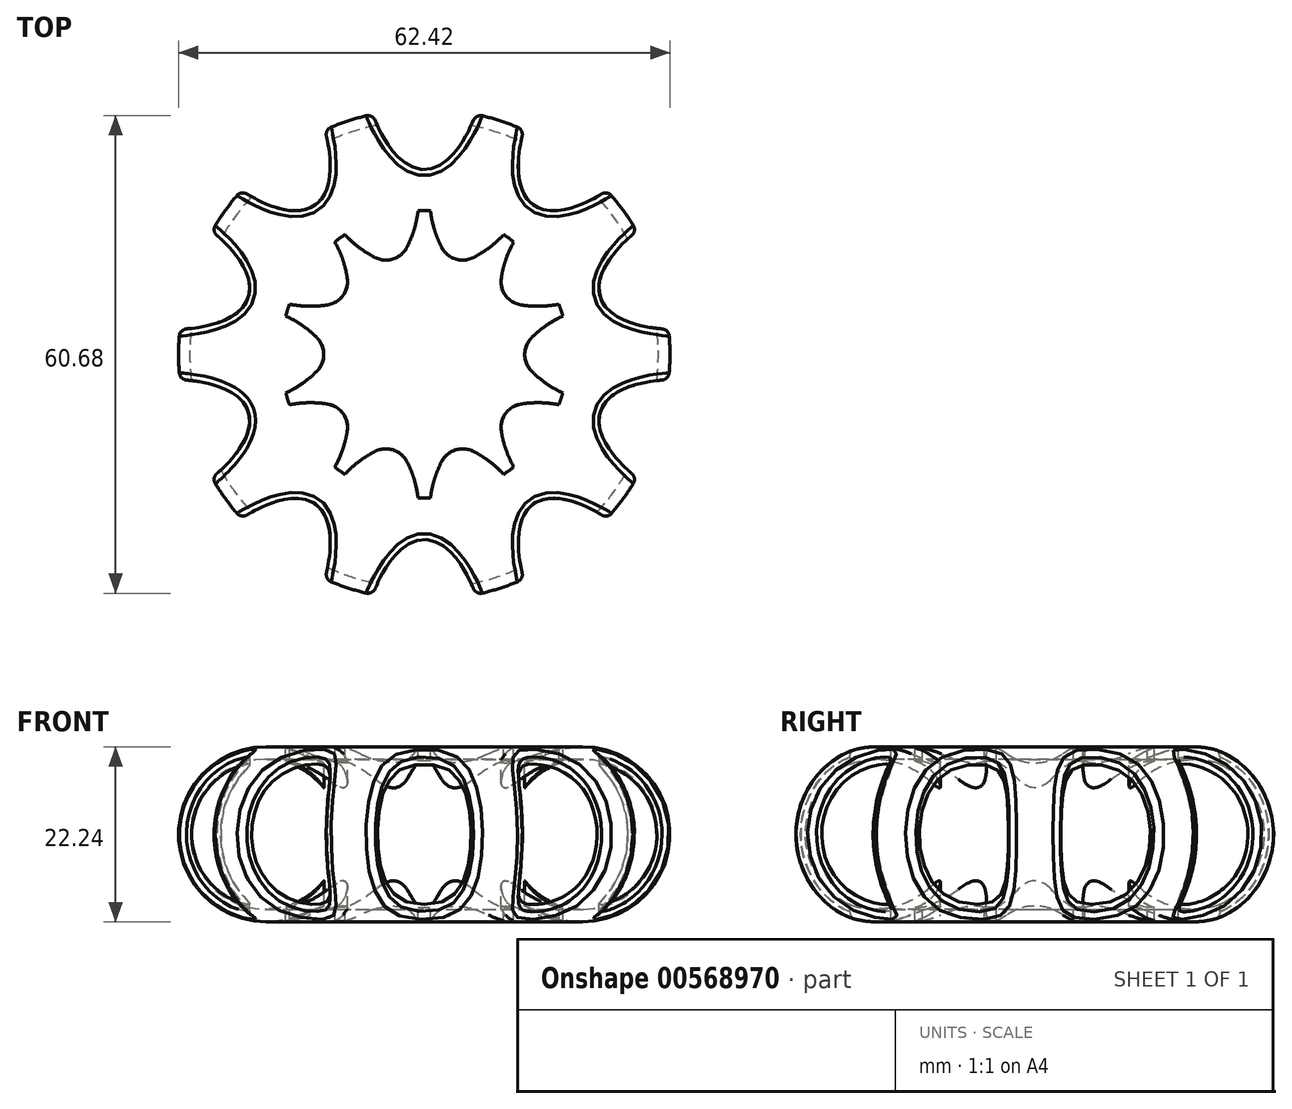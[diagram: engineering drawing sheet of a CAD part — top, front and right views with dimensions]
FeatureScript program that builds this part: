
annotation { "Feature Type Name" : "Feature", "Feature Type Description" : "" }
export const myFeature = defineFeature(function(context is Context, id is Id, definition is map)
    precondition{}
    {
        {
            var Q0;
            Q0=qCreatedBy(makeId("Front.planeOp"),FACE);
            var sketch = newSketch(context, id + "F0", { "sketchPlane" : qUnion([Q0])});
            skArc(sketch, "E0", {"start": v(-15.71, 10.22) * mm, "mid": v(-31.2, 0.04) * mm, "end": v(-15.8, -10.25) * mm});
            skArc(sketch, "E1", {"start": v(-15.71, 10.22) * mm, "mid": v(-8.02, 7.81) * mm, "end": v(0, 7) * mm});
            skArc(sketch, "E2", {"start": v(0, -7) * mm, "mid": v(-8.05, -7.86) * mm, "end": v(-15.8, -10.25) * mm});
            skLineSegment(sketch, "E3", {"start": v(0, -7) * mm, "end": v(0, 7) * mm});
            skSolve(sketch);
        }
        {
            var Q0;
            Q0 = qSketchRegion(id + "F0", true);
            var Q1;
            Q1=sQuery(id+"F0.wireOp",EDGE,"E3");
            revolve(context, id + "F1", {"entities" : qUnion([Q0]), "axis" : qUnion([Q1]), "revolveType" : RevolveType.FULL});
        }
        {
            var Q0;
            Q0=qCreatedBy(makeId("Top.planeOp"),FACE);
            cPlane(context, id + "F2", {"entities" : qUnion([Q0]), "cplaneType" : CPlaneType.OFFSET, "offset" : 12.5 * mm, "width" : 150 * mm, "height" : 150 * mm});
        }
        {
            var Q0;
            Q0=qCreatedBy(id+"F2.planeOp",FACE);
            var sketch = newSketch(context, id + "F3", { "sketchPlane" : qUnion([Q0])});
            skCircle(sketch, "E4", {"center": v(0, 0) * mm, "radius": 18.26 * mm});
            skArc(sketch, "E5", {"start": v(-10.09, 15.22) * mm, "mid": v(-7.15, 12.83) * mm, "end": v(-3.68, 11.32) * mm});
            skArc(sketch, "E6.1.1", {"start": v(-17.1, 6.39) * mm, "mid": v(-13.33, 6.17) * mm, "end": v(-9.63, 7) * mm});
            skArc(sketch, "E6.2.1", {"start": v(-17.6, -4.89) * mm, "mid": v(-14.41, -2.84) * mm, "end": v(-11.9, 0) * mm});
            skArc(sketch, "E6.3.1", {"start": v(-11.36, -14.3) * mm, "mid": v(-9.99, -10.77) * mm, "end": v(-9.63, -7) * mm});
            skArc(sketch, "E6.4.1", {"start": v(-0.79, -18.25) * mm, "mid": v(-1.75, -14.58) * mm, "end": v(-3.68, -11.32) * mm});
            skArc(sketch, "E6.5.1", {"start": v(10.09, -15.22) * mm, "mid": v(7.15, -12.83) * mm, "end": v(3.68, -11.32) * mm});
            skArc(sketch, "E6.6.1", {"start": v(17.1, -6.39) * mm, "mid": v(13.33, -6.17) * mm, "end": v(9.63, -7) * mm});
            skArc(sketch, "E6.7.1", {"start": v(17.6, 4.89) * mm, "mid": v(14.41, 2.84) * mm, "end": v(11.9, 0) * mm});
            skArc(sketch, "E6.8.1", {"start": v(11.36, 14.3) * mm, "mid": v(9.99, 10.77) * mm, "end": v(9.63, 7) * mm});
            skArc(sketch, "E6.9.1", {"start": v(0.79, 18.25) * mm, "mid": v(1.75, 14.58) * mm, "end": v(3.68, 11.32) * mm});
            skArc(sketch, "E7.trimOffspring", {"start": v(-3.68, 11.32) * mm, "mid": v(-1.75, 14.58) * mm, "end": v(-0.79, 18.25) * mm});
            skArc(sketch, "E8.trimOffspring", {"start": v(3.68, 11.32) * mm, "mid": v(7.15, 12.83) * mm, "end": v(10.09, 15.22) * mm});
            skArc(sketch, "E9.trimOffspring", {"start": v(9.63, 7) * mm, "mid": v(13.33, 6.17) * mm, "end": v(17.1, 6.39) * mm});
            skArc(sketch, "E10.trimOffspring", {"start": v(11.9, 0) * mm, "mid": v(14.41, -2.84) * mm, "end": v(17.6, -4.89) * mm});
            skArc(sketch, "E11.trimOffspring", {"start": v(9.63, -7) * mm, "mid": v(9.99, -10.77) * mm, "end": v(11.36, -14.3) * mm});
            skArc(sketch, "E12.trimOffspring", {"start": v(3.68, -11.32) * mm, "mid": v(1.75, -14.58) * mm, "end": v(0.79, -18.25) * mm});
            skArc(sketch, "E13.trimOffspring", {"start": v(-3.68, -11.32) * mm, "mid": v(-7.15, -12.83) * mm, "end": v(-10.09, -15.22) * mm});
            skArc(sketch, "E14.trimOffspring", {"start": v(-9.63, -7) * mm, "mid": v(-13.33, -6.17) * mm, "end": v(-17.1, -6.39) * mm});
            skArc(sketch, "E15.trimOffspring", {"start": v(-11.9, 0) * mm, "mid": v(-14.41, 2.84) * mm, "end": v(-17.6, 4.89) * mm});
            skArc(sketch, "E16.trimOffspring", {"start": v(-9.63, 7) * mm, "mid": v(-9.99, 10.77) * mm, "end": v(-11.36, 14.3) * mm});
            skSolve(sketch);
        }
        {
            var Q0;
            {var subQ7=sQuery(id+"F3.wireOp",EDGE,"E5");Q0=makeQuery(id+"F3.imprint","IMPRINT",FACE,{"disambiguationData":[TD([[makeQuery(id+"F3.imprint","IMPRINT",EDGE,{"derivedFrom":subQ7}),-1.0]])]});}
            extrude(context, id + "F4", {"entities" : qUnion([Q0]), "operationType" : NewBodyOperationType.REMOVE, "oppositeDirection" : true, "depth" : 25 * mm, "offsetDistance" : 25 * mm});
        }
        {
            var Q0;
            Q0=qCreatedBy(id+"F2.planeOp",FACE);
            var sketch = newSketch(context, id + "F5", { "sketchPlane" : qUnion([Q0])});
            skCircle(sketch, "E17", {"center": v(0, 0) * mm, "radius": 31.42 * mm});
            skEllipticalArc(sketch, "E18", {});
            skEllipticalArc(sketch, "E19.1.0", {});
            skEllipticalArc(sketch, "E19.2.0", {});
            skEllipticalArc(sketch, "E19.3.0", {});
            skEllipticalArc(sketch, "E19.4.0", {});
            skEllipticalArc(sketch, "E19.5.0", {});
            skEllipticalArc(sketch, "E19.6.0", {});
            skEllipticalArc(sketch, "E19.7.0", {});
            skEllipticalArc(sketch, "E19.8.0", {});
            skEllipticalArc(sketch, "E19.9.0", {});
            const initialGuessF5  = {"E18": [0, 0.04669829085469246, 0, -1, 0.02319059520959854, 0.009151522777861269, 5.472659938660135, 0.8105253685194521], "E19.1.0": [-0.0274485666716527, 0.03777971090971039, 0.5877852522924731, -0.8090169943749475, 0.02319059520959854, 0.009151522777861269, 5.472659938660135, 0.8105253685194521], "E19.2.0": [-0.04441271381720164, 0.01443056548236416, 0.9510565162951538, -0.3090169943749475, 0.02319059520959854, 0.009151522777861269, 5.472659938660135, 0.8105253685194521], "E19.3.0": [-0.044412713817201646, -0.014430565482364155, 0.9510565162951536, 0.30901699437494734, 0.02319059520959854, 0.009151522777861269, 5.472659938660135, 0.8105253685194521], "E19.4.0": [-0.027448566671652703, -0.037779710909710384, 0.5877852522924732, 0.8090169943749473, 0.02319059520959854, 0.009151522777861269, 5.472659938660135, 0.8105253685194521], "E19.5.0": [0, -0.04669829085469246, 0, 1, 0.02319059520959854, 0.009151522777861269, 5.472659938660135, 0.8105253685194521], "E19.6.0": [0.027448566671652692, -0.03777971090971039, -0.587785252292473, 0.8090169943749476, 0.02319059520959854, 0.009151522777861269, 5.472659938660135, 0.8105253685194521], "E19.7.0": [0.04441271381720164, -0.014430565482364165, -0.9510565162951535, 0.30901699437494756, 0.02319059520959854, 0.009151522777861269, 5.472659938660135, 0.8105253685194521], "E19.8.0": [0.044412713817201646, 0.01443056548236415, -0.9510565162951536, -0.30901699437494723, 0.02319059520959854, 0.009151522777861269, 5.472659938660135, 0.8105253685194521], "E19.9.0": [0.02744856667165271, 0.037779710909710384, -0.5877852522924734, -0.8090169943749473, 0.02319059520959854, 0.009151522777861269, 5.472659938660135, 0.8105253685194521]};
            skSetInitialGuess(sketch, initialGuessF5);
            skSolve(sketch);
        }
        {
            var Q0;
            {var subQ0=sQuery(id+"F5.wireOp",EDGE,"E18");Q0=makeQuery(id+"F5.imprint","IMPRINT",FACE,{"disambiguationData":[TD([[makeQuery(id+"F5.imprint","IMPRINT",EDGE,{"derivedFrom":subQ0}),1.0]])]});}
            var Q1;
            {var subQ0=sQuery(id+"F5.wireOp",EDGE,"E19.9.0");Q1=makeQuery(id+"F5.imprint","IMPRINT",FACE,{"disambiguationData":[TD([[makeQuery(id+"F5.imprint","IMPRINT",EDGE,{"derivedFrom":subQ0}),1.0]])]});}
            var Q2;
            {var subQ0=sQuery(id+"F5.wireOp",EDGE,"E19.8.0");Q2=makeQuery(id+"F5.imprint","IMPRINT",FACE,{"disambiguationData":[TD([[makeQuery(id+"F5.imprint","IMPRINT",EDGE,{"derivedFrom":subQ0}),1.0]])]});}
            var Q3;
            {var subQ0=sQuery(id+"F5.wireOp",EDGE,"E19.7.0");Q3=makeQuery(id+"F5.imprint","IMPRINT",FACE,{"disambiguationData":[TD([[makeQuery(id+"F5.imprint","IMPRINT",EDGE,{"derivedFrom":subQ0}),1.0]])]});}
            var Q4;
            {var subQ0=sQuery(id+"F5.wireOp",EDGE,"E19.6.0");Q4=makeQuery(id+"F5.imprint","IMPRINT",FACE,{"disambiguationData":[TD([[makeQuery(id+"F5.imprint","IMPRINT",EDGE,{"derivedFrom":subQ0}),1.0]])]});}
            var Q5;
            {var subQ0=sQuery(id+"F5.wireOp",EDGE,"E19.5.0");Q5=makeQuery(id+"F5.imprint","IMPRINT",FACE,{"disambiguationData":[TD([[makeQuery(id+"F5.imprint","IMPRINT",EDGE,{"derivedFrom":subQ0}),1.0]])]});}
            var Q6;
            {var subQ0=sQuery(id+"F5.wireOp",EDGE,"E19.4.0");Q6=makeQuery(id+"F5.imprint","IMPRINT",FACE,{"disambiguationData":[TD([[makeQuery(id+"F5.imprint","IMPRINT",EDGE,{"derivedFrom":subQ0}),1.0]])]});}
            var Q7;
            {var subQ0=sQuery(id+"F5.wireOp",EDGE,"E19.3.0");Q7=makeQuery(id+"F5.imprint","IMPRINT",FACE,{"disambiguationData":[TD([[makeQuery(id+"F5.imprint","IMPRINT",EDGE,{"derivedFrom":subQ0}),1.0]])]});}
            var Q8;
            {var subQ0=sQuery(id+"F5.wireOp",EDGE,"E19.2.0");Q8=makeQuery(id+"F5.imprint","IMPRINT",FACE,{"disambiguationData":[TD([[makeQuery(id+"F5.imprint","IMPRINT",EDGE,{"derivedFrom":subQ0}),1.0]])]});}
            var Q9;
            {var subQ0=sQuery(id+"F5.wireOp",EDGE,"E19.1.0");Q9=makeQuery(id+"F5.imprint","IMPRINT",FACE,{"disambiguationData":[TD([[makeQuery(id+"F5.imprint","IMPRINT",EDGE,{"derivedFrom":subQ0}),1.0]])]});}
            extrude(context, id + "F6", {"entities" : qUnion([Q0, Q1, Q2, Q3, Q4, Q5, Q6, Q7, Q8, Q9]), "operationType" : NewBodyOperationType.REMOVE, "oppositeDirection" : true, "depth" : 25 * mm, "offsetDistance" : 25 * mm});
        }
        {
            var Q0;
            Q0=qCreatedBy(makeId("Front.planeOp"),FACE);
            var sketch = newSketch(context, id + "F7", { "sketchPlane" : qUnion([Q0])});
            skCircle(sketch, "E20", {"center": v(-20.22, 0) * mm, "radius": 9.51 * mm});
            skSolve(sketch);
        }
        {
            var Q0;
            Q0 = qSketchRegion(id + "F7", true);
            var Q1;
            Q1=sQuery(id+"F0.wireOp",EDGE,"E3");
            revolve(context, id + "F8", {"operationType" : NewBodyOperationType.REMOVE, "entities" : qUnion([Q0]), "axis" : qUnion([Q1]), "revolveType" : RevolveType.FULL});
        }
        {
            var Q0;
            Q0=makeQuery(id+"F6.boolean.opBoolean","INTERSECT",EDGE,{"derivedFrom":[makeQuery(id+"F1.opRevolve","SWEPT_FACE",FACE,{"disambiguationData":[OSD([sQuery(id+"F0.wireOp",EDGE,"E0")])]}),makeQuery(id+"F6.opExtrude","SWEPT_FACE",FACE,{"disambiguationData":[OSD([sQuery(id+"F5.wireOp",EDGE,"E19.6.0")])]})]});
            var Q1;
            Q1=makeQuery(id+"F6.boolean.opBoolean","INTERSECT",EDGE,{"derivedFrom":[makeQuery(id+"F1.opRevolve","SWEPT_FACE",FACE,{"disambiguationData":[OSD([sQuery(id+"F0.wireOp",EDGE,"E0")])]}),makeQuery(id+"F6.opExtrude","SWEPT_FACE",FACE,{"disambiguationData":[OSD([sQuery(id+"F5.wireOp",EDGE,"E19.5.0")])]})]});
            var Q2;
            Q2=makeQuery(id+"F6.boolean.opBoolean","INTERSECT",EDGE,{"derivedFrom":[makeQuery(id+"F1.opRevolve","SWEPT_FACE",FACE,{"disambiguationData":[OSD([sQuery(id+"F0.wireOp",EDGE,"E0")])]}),makeQuery(id+"F6.opExtrude","SWEPT_FACE",FACE,{"disambiguationData":[OSD([sQuery(id+"F5.wireOp",EDGE,"E19.4.0")])]})]});
            var Q3;
            Q3=makeQuery(id+"F6.boolean.opBoolean","INTERSECT",EDGE,{"derivedFrom":[makeQuery(id+"F1.opRevolve","SWEPT_FACE",FACE,{"disambiguationData":[OSD([sQuery(id+"F0.wireOp",EDGE,"E0")])]}),makeQuery(id+"F6.opExtrude","SWEPT_FACE",FACE,{"disambiguationData":[OSD([sQuery(id+"F5.wireOp",EDGE,"E19.3.0")])]})]});
            var Q4;
            Q4=makeQuery(id+"F6.boolean.opBoolean","INTERSECT",EDGE,{"derivedFrom":[makeQuery(id+"F1.opRevolve","SWEPT_FACE",FACE,{"disambiguationData":[OSD([sQuery(id+"F0.wireOp",EDGE,"E0")])]}),makeQuery(id+"F6.opExtrude","SWEPT_FACE",FACE,{"disambiguationData":[OSD([sQuery(id+"F5.wireOp",EDGE,"E19.2.0")])]})]});
            var Q5;
            Q5=makeQuery(id+"F6.boolean.opBoolean","INTERSECT",EDGE,{"derivedFrom":[makeQuery(id+"F1.opRevolve","SWEPT_FACE",FACE,{"disambiguationData":[OSD([sQuery(id+"F0.wireOp",EDGE,"E0")])]}),makeQuery(id+"F6.opExtrude","SWEPT_FACE",FACE,{"disambiguationData":[OSD([sQuery(id+"F5.wireOp",EDGE,"E19.1.0")])]})]});
            var Q6;
            Q6=makeQuery(id+"F6.boolean.opBoolean","INTERSECT",EDGE,{"derivedFrom":[makeQuery(id+"F1.opRevolve","SWEPT_FACE",FACE,{"disambiguationData":[OSD([sQuery(id+"F0.wireOp",EDGE,"E0")])]}),makeQuery(id+"F6.opExtrude","SWEPT_FACE",FACE,{"disambiguationData":[OSD([sQuery(id+"F5.wireOp",EDGE,"E18")])]})]});
            var Q7;
            Q7=makeQuery(id+"F6.boolean.opBoolean","INTERSECT",EDGE,{"derivedFrom":[makeQuery(id+"F1.opRevolve","SWEPT_FACE",FACE,{"disambiguationData":[OSD([sQuery(id+"F0.wireOp",EDGE,"E0")])]}),makeQuery(id+"F6.opExtrude","SWEPT_FACE",FACE,{"disambiguationData":[OSD([sQuery(id+"F5.wireOp",EDGE,"E19.9.0")])]})]});
            var Q8;
            Q8=makeQuery(id+"F6.boolean.opBoolean","INTERSECT",EDGE,{"derivedFrom":[makeQuery(id+"F1.opRevolve","SWEPT_FACE",FACE,{"disambiguationData":[OSD([sQuery(id+"F0.wireOp",EDGE,"E0")])]}),makeQuery(id+"F6.opExtrude","SWEPT_FACE",FACE,{"disambiguationData":[OSD([sQuery(id+"F5.wireOp",EDGE,"E19.8.0")])]})]});
            var Q9;
            Q9=makeQuery(id+"F6.boolean.opBoolean","INTERSECT",EDGE,{"derivedFrom":[makeQuery(id+"F1.opRevolve","SWEPT_FACE",FACE,{"disambiguationData":[OSD([sQuery(id+"F0.wireOp",EDGE,"E0")])]}),makeQuery(id+"F6.opExtrude","SWEPT_FACE",FACE,{"disambiguationData":[OSD([sQuery(id+"F5.wireOp",EDGE,"E19.7.0")])]})]});
            fillet(context, id + "F9", {"entities" : qUnion([Q0, Q1, Q2, Q3, Q4, Q5, Q6, Q7, Q8, Q9]), "radius" : 1 * mm, "tangentPropagation" : true, "allowEdgeOverflow" : false});
        }
        {
            var Q0;
            {var subQ0=sQuery(id+"F3.wireOp",EDGE,"E6.3.1");var subQ1=sQuery(id+"F3.wireOp",EDGE,"E14.trimOffspring");Q0=makeQuery(id+"F8.boolean.opBoolean","SPLIT",EDGE,{"disambiguationData":[TD([makeQuery(id+"F1.opRevolve","SWEPT_FACE",FACE,{"disambiguationData":[OSD([sQuery(id+"F0.wireOp",EDGE,"E1")])]})])],"derivedFrom":makeQuery(id+"F4.boolean.opBoolean","COPY",EDGE,{"derivedFrom":makeQuery(id+"F4.opExtrude","SWEPT_EDGE",EDGE,{"disambiguationData":[OSD([subQ0,subQ1])]})})});}
            var Q1;
            {var subQ0=sQuery(id+"F3.wireOp",EDGE,"E13.trimOffspring");var subQ1=sQuery(id+"F3.wireOp",EDGE,"E6.4.1");Q1=makeQuery(id+"F8.boolean.opBoolean","SPLIT",EDGE,{"disambiguationData":[TD([makeQuery(id+"F1.opRevolve","SWEPT_FACE",FACE,{"disambiguationData":[OSD([sQuery(id+"F0.wireOp",EDGE,"E1")])]})])],"derivedFrom":makeQuery(id+"F4.boolean.opBoolean","COPY",EDGE,{"derivedFrom":makeQuery(id+"F4.opExtrude","SWEPT_EDGE",EDGE,{"disambiguationData":[OSD([subQ1,subQ0])]})})});}
            var Q2;
            {var subQ0=sQuery(id+"F3.wireOp",EDGE,"E6.2.1");var subQ1=sQuery(id+"F3.wireOp",EDGE,"E15.trimOffspring");Q2=makeQuery(id+"F8.boolean.opBoolean","SPLIT",EDGE,{"disambiguationData":[TD([makeQuery(id+"F1.opRevolve","SWEPT_FACE",FACE,{"disambiguationData":[OSD([sQuery(id+"F0.wireOp",EDGE,"E1")])]})])],"derivedFrom":makeQuery(id+"F4.boolean.opBoolean","COPY",EDGE,{"derivedFrom":makeQuery(id+"F4.opExtrude","SWEPT_EDGE",EDGE,{"disambiguationData":[OSD([subQ0,subQ1])]})})});}
            var Q3;
            {var subQ0=sQuery(id+"F3.wireOp",EDGE,"E6.1.1");var subQ1=sQuery(id+"F3.wireOp",EDGE,"E16.trimOffspring");Q3=makeQuery(id+"F8.boolean.opBoolean","SPLIT",EDGE,{"disambiguationData":[TD([makeQuery(id+"F1.opRevolve","SWEPT_FACE",FACE,{"disambiguationData":[OSD([sQuery(id+"F0.wireOp",EDGE,"E1")])]})])],"derivedFrom":makeQuery(id+"F4.boolean.opBoolean","COPY",EDGE,{"derivedFrom":makeQuery(id+"F4.opExtrude","SWEPT_EDGE",EDGE,{"disambiguationData":[OSD([subQ0,subQ1])]})})});}
            var Q4;
            {var subQ0=sQuery(id+"F3.wireOp",EDGE,"E5");var subQ1=sQuery(id+"F3.wireOp",EDGE,"E7.trimOffspring");Q4=makeQuery(id+"F8.boolean.opBoolean","SPLIT",EDGE,{"disambiguationData":[TD([makeQuery(id+"F1.opRevolve","SWEPT_FACE",FACE,{"disambiguationData":[OSD([sQuery(id+"F0.wireOp",EDGE,"E1")])]})])],"derivedFrom":makeQuery(id+"F4.boolean.opBoolean","COPY",EDGE,{"derivedFrom":makeQuery(id+"F4.opExtrude","SWEPT_EDGE",EDGE,{"disambiguationData":[OSD([subQ0,subQ1])]})})});}
            var Q5;
            {var subQ0=sQuery(id+"F3.wireOp",EDGE,"E8.trimOffspring");var subQ1=sQuery(id+"F3.wireOp",EDGE,"E6.9.1");Q5=makeQuery(id+"F8.boolean.opBoolean","SPLIT",EDGE,{"disambiguationData":[TD([makeQuery(id+"F1.opRevolve","SWEPT_FACE",FACE,{"disambiguationData":[OSD([sQuery(id+"F0.wireOp",EDGE,"E1")])]})])],"derivedFrom":makeQuery(id+"F4.boolean.opBoolean","COPY",EDGE,{"derivedFrom":makeQuery(id+"F4.opExtrude","SWEPT_EDGE",EDGE,{"disambiguationData":[OSD([subQ1,subQ0])]})})});}
            var Q6;
            {var subQ0=sQuery(id+"F3.wireOp",EDGE,"E6.8.1");var subQ1=sQuery(id+"F3.wireOp",EDGE,"E9.trimOffspring");Q6=makeQuery(id+"F8.boolean.opBoolean","SPLIT",EDGE,{"disambiguationData":[TD([makeQuery(id+"F1.opRevolve","SWEPT_FACE",FACE,{"disambiguationData":[OSD([sQuery(id+"F0.wireOp",EDGE,"E1")])]})])],"derivedFrom":makeQuery(id+"F4.boolean.opBoolean","COPY",EDGE,{"derivedFrom":makeQuery(id+"F4.opExtrude","SWEPT_EDGE",EDGE,{"disambiguationData":[OSD([subQ0,subQ1])]})})});}
            var Q7;
            {var subQ0=sQuery(id+"F3.wireOp",EDGE,"E6.7.1");var subQ1=sQuery(id+"F3.wireOp",EDGE,"E10.trimOffspring");Q7=makeQuery(id+"F8.boolean.opBoolean","SPLIT",EDGE,{"disambiguationData":[TD([makeQuery(id+"F1.opRevolve","SWEPT_FACE",FACE,{"disambiguationData":[OSD([sQuery(id+"F0.wireOp",EDGE,"E1")])]})])],"derivedFrom":makeQuery(id+"F4.boolean.opBoolean","COPY",EDGE,{"derivedFrom":makeQuery(id+"F4.opExtrude","SWEPT_EDGE",EDGE,{"disambiguationData":[OSD([subQ0,subQ1])]})})});}
            var Q8;
            {var subQ0=sQuery(id+"F3.wireOp",EDGE,"E6.6.1");var subQ1=sQuery(id+"F3.wireOp",EDGE,"E11.trimOffspring");Q8=makeQuery(id+"F8.boolean.opBoolean","SPLIT",EDGE,{"disambiguationData":[TD([makeQuery(id+"F1.opRevolve","SWEPT_FACE",FACE,{"disambiguationData":[OSD([sQuery(id+"F0.wireOp",EDGE,"E1")])]})])],"derivedFrom":makeQuery(id+"F4.boolean.opBoolean","COPY",EDGE,{"derivedFrom":makeQuery(id+"F4.opExtrude","SWEPT_EDGE",EDGE,{"disambiguationData":[OSD([subQ0,subQ1])]})})});}
            var Q9;
            {var subQ0=sQuery(id+"F3.wireOp",EDGE,"E6.5.1");var subQ1=sQuery(id+"F3.wireOp",EDGE,"E12.trimOffspring");Q9=makeQuery(id+"F8.boolean.opBoolean","SPLIT",EDGE,{"disambiguationData":[TD([makeQuery(id+"F1.opRevolve","SWEPT_FACE",FACE,{"disambiguationData":[OSD([sQuery(id+"F0.wireOp",EDGE,"E1")])]})])],"derivedFrom":makeQuery(id+"F4.boolean.opBoolean","COPY",EDGE,{"derivedFrom":makeQuery(id+"F4.opExtrude","SWEPT_EDGE",EDGE,{"disambiguationData":[OSD([subQ0,subQ1])]})})});}
            var Q10;
            {var subQ0=sQuery(id+"F3.wireOp",EDGE,"E6.7.1");var subQ1=sQuery(id+"F3.wireOp",EDGE,"E10.trimOffspring");Q10=makeQuery(id+"F8.boolean.opBoolean","SPLIT",EDGE,{"disambiguationData":[TD([makeQuery(id+"F1.opRevolve","SWEPT_FACE",FACE,{"disambiguationData":[OSD([sQuery(id+"F0.wireOp",EDGE,"E2")])]})])],"derivedFrom":makeQuery(id+"F4.boolean.opBoolean","COPY",EDGE,{"derivedFrom":makeQuery(id+"F4.opExtrude","SWEPT_EDGE",EDGE,{"disambiguationData":[OSD([subQ0,subQ1])]})})});}
            var Q11;
            {var subQ0=sQuery(id+"F3.wireOp",EDGE,"E6.6.1");var subQ1=sQuery(id+"F3.wireOp",EDGE,"E11.trimOffspring");Q11=makeQuery(id+"F8.boolean.opBoolean","SPLIT",EDGE,{"disambiguationData":[TD([makeQuery(id+"F1.opRevolve","SWEPT_FACE",FACE,{"disambiguationData":[OSD([sQuery(id+"F0.wireOp",EDGE,"E2")])]})])],"derivedFrom":makeQuery(id+"F4.boolean.opBoolean","COPY",EDGE,{"derivedFrom":makeQuery(id+"F4.opExtrude","SWEPT_EDGE",EDGE,{"disambiguationData":[OSD([subQ0,subQ1])]})})});}
            var Q12;
            {var subQ0=sQuery(id+"F3.wireOp",EDGE,"E6.5.1");var subQ1=sQuery(id+"F3.wireOp",EDGE,"E12.trimOffspring");Q12=makeQuery(id+"F8.boolean.opBoolean","SPLIT",EDGE,{"disambiguationData":[TD([makeQuery(id+"F1.opRevolve","SWEPT_FACE",FACE,{"disambiguationData":[OSD([sQuery(id+"F0.wireOp",EDGE,"E2")])]})])],"derivedFrom":makeQuery(id+"F4.boolean.opBoolean","COPY",EDGE,{"derivedFrom":makeQuery(id+"F4.opExtrude","SWEPT_EDGE",EDGE,{"disambiguationData":[OSD([subQ0,subQ1])]})})});}
            var Q13;
            {var subQ0=sQuery(id+"F3.wireOp",EDGE,"E9.trimOffspring");var subQ1=sQuery(id+"F3.wireOp",EDGE,"E6.8.1");Q13=makeQuery(id+"F8.boolean.opBoolean","SPLIT",EDGE,{"disambiguationData":[TD([makeQuery(id+"F1.opRevolve","SWEPT_FACE",FACE,{"disambiguationData":[OSD([sQuery(id+"F0.wireOp",EDGE,"E2")])]})])],"derivedFrom":makeQuery(id+"F4.boolean.opBoolean","COPY",EDGE,{"derivedFrom":makeQuery(id+"F4.opExtrude","SWEPT_EDGE",EDGE,{"disambiguationData":[OSD([subQ1,subQ0])]})})});}
            var Q14;
            {var subQ0=sQuery(id+"F3.wireOp",EDGE,"E6.9.1");var subQ1=sQuery(id+"F3.wireOp",EDGE,"E8.trimOffspring");Q14=makeQuery(id+"F8.boolean.opBoolean","SPLIT",EDGE,{"disambiguationData":[TD([makeQuery(id+"F1.opRevolve","SWEPT_FACE",FACE,{"disambiguationData":[OSD([sQuery(id+"F0.wireOp",EDGE,"E2")])]})])],"derivedFrom":makeQuery(id+"F4.boolean.opBoolean","COPY",EDGE,{"derivedFrom":makeQuery(id+"F4.opExtrude","SWEPT_EDGE",EDGE,{"disambiguationData":[OSD([subQ0,subQ1])]})})});}
            var Q15;
            {var subQ0=sQuery(id+"F3.wireOp",EDGE,"E6.4.1");var subQ1=sQuery(id+"F3.wireOp",EDGE,"E13.trimOffspring");Q15=makeQuery(id+"F8.boolean.opBoolean","SPLIT",EDGE,{"disambiguationData":[TD([makeQuery(id+"F1.opRevolve","SWEPT_FACE",FACE,{"disambiguationData":[OSD([sQuery(id+"F0.wireOp",EDGE,"E2")])]})])],"derivedFrom":makeQuery(id+"F4.boolean.opBoolean","COPY",EDGE,{"derivedFrom":makeQuery(id+"F4.opExtrude","SWEPT_EDGE",EDGE,{"disambiguationData":[OSD([subQ0,subQ1])]})})});}
            var Q16;
            {var subQ0=sQuery(id+"F3.wireOp",EDGE,"E14.trimOffspring");var subQ1=sQuery(id+"F3.wireOp",EDGE,"E6.3.1");Q16=makeQuery(id+"F8.boolean.opBoolean","SPLIT",EDGE,{"disambiguationData":[TD([makeQuery(id+"F1.opRevolve","SWEPT_FACE",FACE,{"disambiguationData":[OSD([sQuery(id+"F0.wireOp",EDGE,"E2")])]})])],"derivedFrom":makeQuery(id+"F4.boolean.opBoolean","COPY",EDGE,{"derivedFrom":makeQuery(id+"F4.opExtrude","SWEPT_EDGE",EDGE,{"disambiguationData":[OSD([subQ1,subQ0])]})})});}
            var Q17;
            {var subQ0=sQuery(id+"F3.wireOp",EDGE,"E6.2.1");var subQ1=sQuery(id+"F3.wireOp",EDGE,"E15.trimOffspring");Q17=makeQuery(id+"F8.boolean.opBoolean","SPLIT",EDGE,{"disambiguationData":[TD([makeQuery(id+"F1.opRevolve","SWEPT_FACE",FACE,{"disambiguationData":[OSD([sQuery(id+"F0.wireOp",EDGE,"E2")])]})])],"derivedFrom":makeQuery(id+"F4.boolean.opBoolean","COPY",EDGE,{"derivedFrom":makeQuery(id+"F4.opExtrude","SWEPT_EDGE",EDGE,{"disambiguationData":[OSD([subQ0,subQ1])]})})});}
            var Q18;
            {var subQ0=sQuery(id+"F3.wireOp",EDGE,"E6.1.1");var subQ1=sQuery(id+"F3.wireOp",EDGE,"E16.trimOffspring");Q18=makeQuery(id+"F8.boolean.opBoolean","SPLIT",EDGE,{"disambiguationData":[TD([makeQuery(id+"F1.opRevolve","SWEPT_FACE",FACE,{"disambiguationData":[OSD([sQuery(id+"F0.wireOp",EDGE,"E2")])]})])],"derivedFrom":makeQuery(id+"F4.boolean.opBoolean","COPY",EDGE,{"derivedFrom":makeQuery(id+"F4.opExtrude","SWEPT_EDGE",EDGE,{"disambiguationData":[OSD([subQ0,subQ1])]})})});}
            var Q19;
            {var subQ0=sQuery(id+"F3.wireOp",EDGE,"E5");var subQ1=sQuery(id+"F3.wireOp",EDGE,"E7.trimOffspring");Q19=makeQuery(id+"F8.boolean.opBoolean","SPLIT",EDGE,{"disambiguationData":[TD([makeQuery(id+"F1.opRevolve","SWEPT_FACE",FACE,{"disambiguationData":[OSD([sQuery(id+"F0.wireOp",EDGE,"E2")])]})])],"derivedFrom":makeQuery(id+"F4.boolean.opBoolean","COPY",EDGE,{"derivedFrom":makeQuery(id+"F4.opExtrude","SWEPT_EDGE",EDGE,{"disambiguationData":[OSD([subQ0,subQ1])]})})});}
            fillet(context, id + "F10", {"entities" : qUnion([Q0, Q1, Q2, Q3, Q4, Q5, Q6, Q7, Q8, Q9, Q10, Q11, Q12, Q13, Q14, Q15, Q16, Q17, Q18, Q19]), "radius" : 3 * mm, "tangentPropagation" : true, "allowEdgeOverflow" : false});
        }
    });
